# Revit family: RN 24022 Valvola di regolazione
name_source: partatom
category: Rohrzubehör
units: mm (PartAtom-declared; Revit-internal decimal feet)

## family parameters
Arbeitsebenenbasiert = Nein
Beim Laden mit Abzugskörper schneiden = Nein
Bemaßung runder Anschluss = Durchmesser verwenden
Gemeinsam genutzt = Nein
Immer vertikal = Ja
Teiletyp = Ventil - Zerlegung in

## types (3) — shared parameters
1.010.00.2 Blattnummer der Richtlinie = 17
1.010.00.3 Ausgabedatum (Monat) der Richtlinie = 201601
1.010.00.4 Herstellername = R. Nussbaum AG
1.010.00.5 Revisionsdatum der Datei = 20190528
1.010.00.6 Webadresse des Herstellers = http://www.nussbaum.ch
1.100.00.3 Sortiernummer für Anzeigereihenfolge = 2
1.100.00.4 Produktbezeichnung = Regulierarmaturen (Drosselarmaturen)
1.960/3L.00.8 Link (URL) = https://www.nussbaum.ch
17.700.00.4 Armaturentyp = 2
17.700.00.7 Maximale Betriebstemperatur TB [°C] = 90
17.700.00.8 Maximaler Betriebsdruck (Arbeitsdruck) ps [1.0 · 105 Pa] = 16
Connector Visibility = Nein
EnclosingSpace Visibility = Nein
Hersteller = R. Nussbauzm AG
URL = https://www.nussbaum.ch

## per-type parameters (varying)
| type | 1.800.00.3 TGA-Nummer | 1.810.00.3 Hersteller-Bestellnummer | 1.810.00.4 DATANORM-Nummer | 1.810.00.5 StLB-Nummer | 1.810.00.6 GTIN-Nummer | 17.700.00.30 Produktbeschreibung | 17.700.00.5 Nennweite DN | 17.700.00.6 kvs-Wert [m3/h] | CONNECTOR0_DIAMETER_dX_0r | CONNECTOR0_dX_00 | CONNECTOR0_dX_01 | CONNECTOR0_ref_dX | CONNECTOR1_DIAMETER_dX_0r | CONNECTOR1_dX_00 | CONNECTOR1_dX_01 | CONNECTOR1_ref_dX | Modell | R. Nussbaum AG 24022.04 de Visibility | R. Nussbaum AG 24022.05 de Visibility | R. Nussbaum AG 24022.06 de Visibility | Typenkommentare |
| DN 15 | 00200100000000000000000000000200700000000000000001000????? | 24022.04 | 24022.04 | 654.113 | 7612945698131 | 24022.04, Regulierventil, Regulierspindel mit Stellanzeige, DN=15, Rp=½ | 15 | 2.3 | 15 mm | 37 mm | 24 mm | 24 mm | 15 mm | 25 mm  [stored 0.082021 ft] | 38 mm | 25 mm  [stored 0.082021 ft] | 24022.04 | Ja | Nein | Nein | Valvola di regolazioneDN 15 |
| DN 20 | 00200100000000000000000000000200700000000000000002000????? | 24022.05 | 24022.05 | 654.114 | 7612945698148 | 24022.05, Regulierventil, Regulierspindel mit Stellanzeige, DN=20, Rp=¾ | 20 | 3.74 | 20 mm | 40 mm | 25 mm  [stored 0.082021 ft] | 25 mm  [stored 0.082021 ft] | 20 mm | 25 mm  [stored 0.082021 ft] | 40 mm | 25 mm  [stored 0.082021 ft] | 24022.05 | Nein | Ja | Nein | Valvola di regolazioneDN 20 |
| DN 25 | 00200100000000000000000000000200700000000000000003000????? | 24022.06 | 24022.06 | 654.115 | 7612945698155 | 24022.06, Regulierventil, Regulierspindel mit Stellanzeige, DN=25, Rp=1 | 25 | 6.47 | 25 mm  [stored 0.082021 ft] | 42 mm | 25 mm  [stored 0.082021 ft] | 25 mm  [stored 0.082021 ft] | 25 mm  [stored 0.082021 ft] | 26 mm | 43 mm | 26 mm | 24022.06 | Nein | Nein | Ja | Valvola di regolazioneDN 25 |

note: [stored X ft] marks values corroborated as IEEE doubles in the binary element streams (Revit-internal decimal feet)

## geometry (parser evidence)
native form markers: Sweep x2
no freeform markers — native parametric forms only
